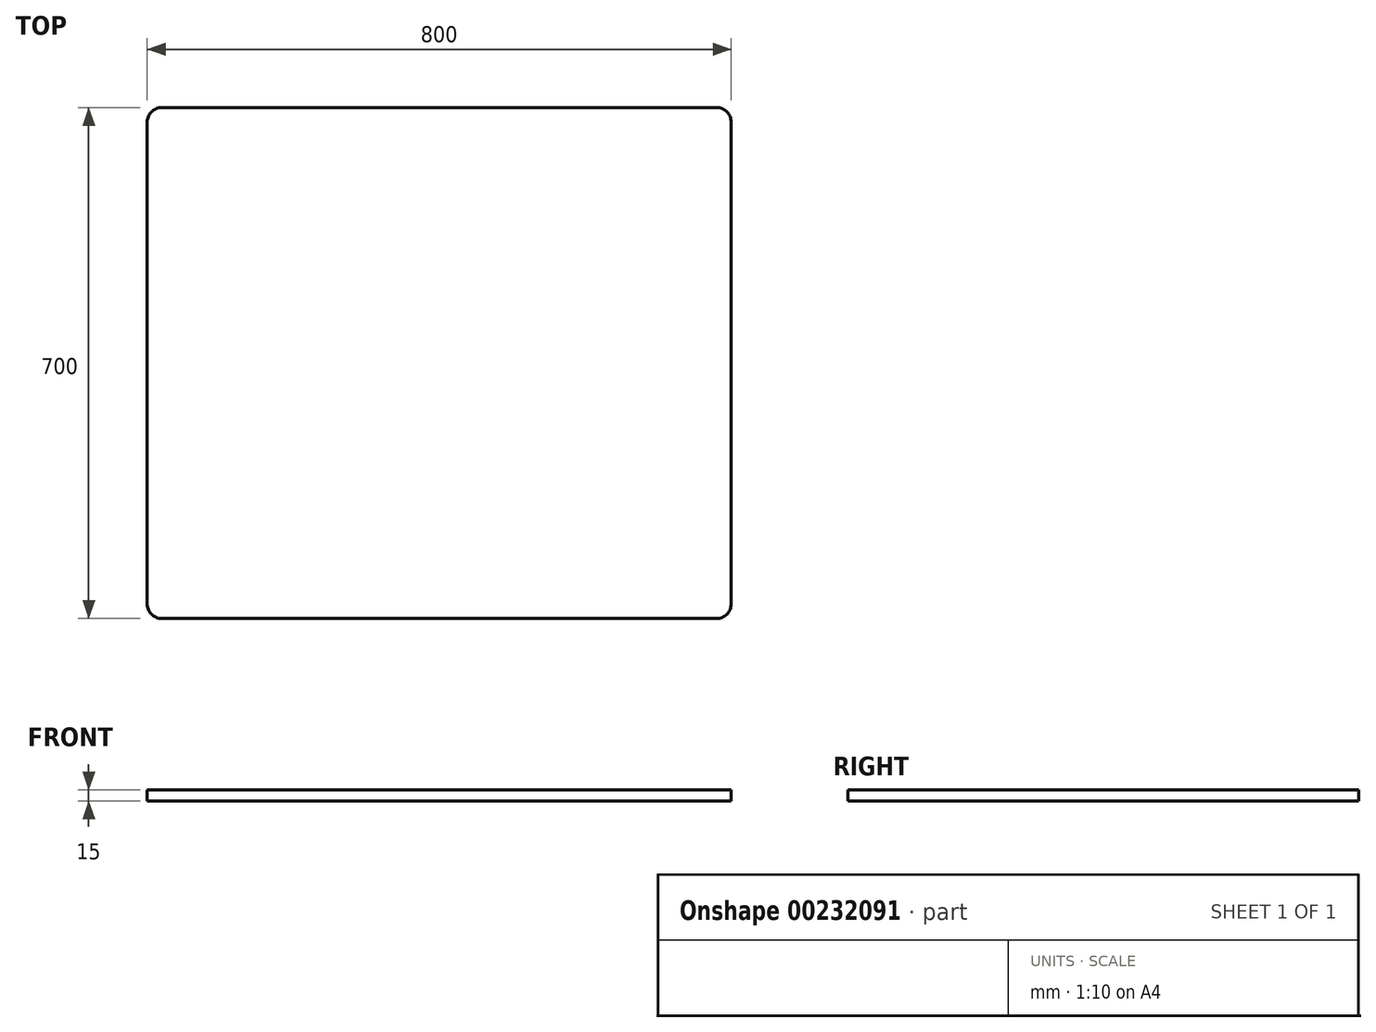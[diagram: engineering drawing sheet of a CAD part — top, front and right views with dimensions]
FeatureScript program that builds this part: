
annotation { "Feature Type Name" : "Feature", "Feature Type Description" : "" }
export const myFeature = defineFeature(function(context is Context, id is Id, definition is map)
    precondition{}
    {
        {
            var Q0;
            Q0=qCreatedBy(makeId("Top.planeOp"),FACE);
            var sketch = newSketch(context, id + "F0", { "sketchPlane" : qUnion([Q0])});
            skLineSegment(sketch, "E0.bottom", {"start": v(-380, 350) * mm, "end": v(380, 350) * mm});
            skLineSegment(sketch, "E0.top", {"start": v(-380, -350) * mm, "end": v(380, -350) * mm});
            skLineSegment(sketch, "E0.left", {"start": v(-400, 330) * mm, "end": v(-400, -330) * mm});
            skLineSegment(sketch, "E0.right", {"start": v(400, 330) * mm, "end": v(400, -330) * mm});
            skPoint(sketch, "E1.visualSharp", {"position": v(-400, 350) * mm});
            skArc(sketch, "E1.filletArc", {"start": v(-380, 350) * mm, "mid": v(-394.14, 344.14) * mm, "end": v(-400, 330) * mm});
            skPoint(sketch, "E2.visualSharp", {"position": v(400, 350) * mm});
            skArc(sketch, "E2.filletArc", {"start": v(400, 330) * mm, "mid": v(394.14, 344.14) * mm, "end": v(380, 350) * mm});
            skPoint(sketch, "E3.visualSharp", {"position": v(400, -350) * mm});
            skArc(sketch, "E3.filletArc", {"start": v(380, -350) * mm, "mid": v(394.14, -344.14) * mm, "end": v(400, -330) * mm});
            skPoint(sketch, "E4.visualSharp", {"position": v(-400, -350) * mm});
            skArc(sketch, "E4.filletArc", {"start": v(-400, -330) * mm, "mid": v(-394.14, -344.14) * mm, "end": v(-380, -350) * mm});
            skSolve(sketch);
        }
        {
            var Q0;
            Q0=makeQuery(id+"F0.imprint","IMPRINT",FACE,{"disambiguationData":[TD([[makeQuery(id+"F0.imprint","IMPRINT",EDGE,{"derivedFrom":sQuery(id+"F0.wireOp",EDGE,"E0.bottom")}),-1.0]])]});
            extrude(context, id + "F1", {"entities" : qUnion([Q0]), "depth" : 15 * mm});
        }
    });
